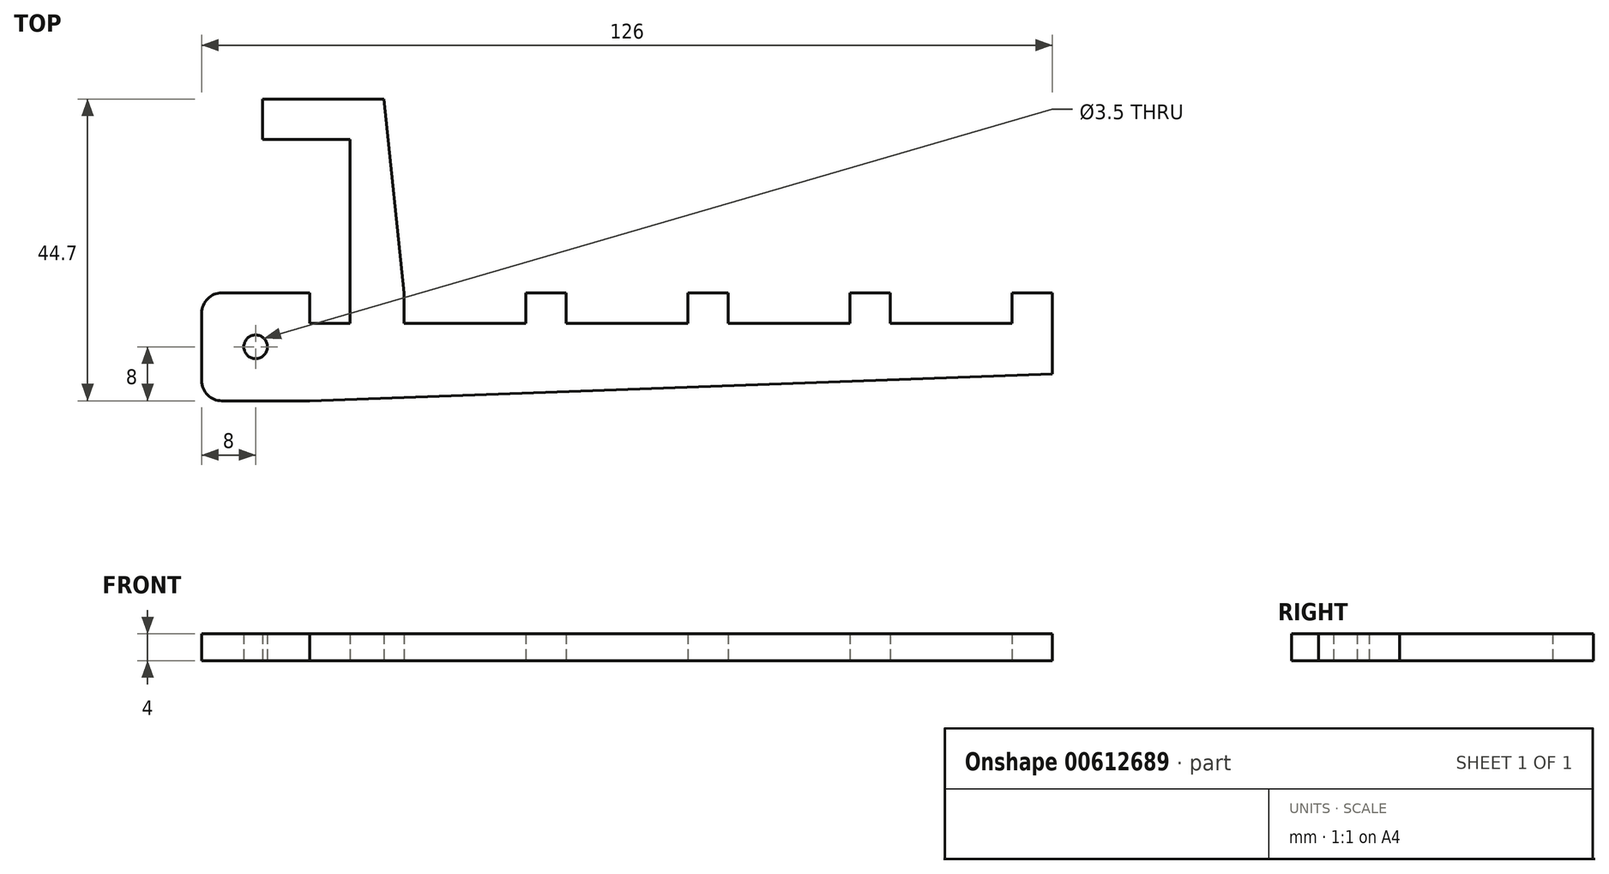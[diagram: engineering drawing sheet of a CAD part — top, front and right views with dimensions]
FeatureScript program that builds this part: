
annotation { "Feature Type Name" : "Feature", "Feature Type Description" : "" }
export const myFeature = defineFeature(function(context is Context, id is Id, definition is map)
    precondition{}
    {
        {
            var Q0;
            Q0=qCreatedBy(makeId("Top.planeOp"),FACE);
            var sketch = newSketch(context, id + "F0", { "sketchPlane" : qUnion([Q0])});
            skLineSegment(sketch, "E0", {"start": v(-36, 22.35) * mm, "end": v(-54, 22.35) * mm});
            skLineSegment(sketch, "E1", {"start": v(-41, 16.35) * mm, "end": v(-54, 16.35) * mm});
            skLineSegment(sketch, "E2", {"start": v(39, -6.35) * mm, "end": v(33, -6.35) * mm});
            skLineSegment(sketch, "E3", {"start": v(63, -6.35) * mm, "end": v(57, -6.35) * mm});
            skLineSegment(sketch, "E4", {"start": v(15, -6.35) * mm, "end": v(9, -6.35) * mm});
            skLineSegment(sketch, "E5", {"start": v(-9, -6.35) * mm, "end": v(-15, -6.35) * mm});
            skLineSegment(sketch, "E6", {"start": v(-47, -6.35) * mm, "end": v(-60, -6.35) * mm});
            skLineSegment(sketch, "E7", {"start": v(63, -6.35) * mm, "end": v(63, -18.35) * mm});
            skLineSegment(sketch, "E8", {"start": v(-41, 16.35) * mm, "end": v(-41, -10.85) * mm});
            skLineSegment(sketch, "E9", {"start": v(-54, 22.35) * mm, "end": v(-54, 16.35) * mm});
            skLineSegment(sketch, "E10", {"start": v(-36, 22.35) * mm, "end": v(-33, -6.35) * mm});
            skLineSegment(sketch, "E11", {"start": v(33, -10.85) * mm, "end": v(15, -10.85) * mm});
            skLineSegment(sketch, "E12", {"start": v(57, -10.85) * mm, "end": v(39, -10.85) * mm});
            skLineSegment(sketch, "E13", {"start": v(9, -10.85) * mm, "end": v(-9, -10.85) * mm});
            skLineSegment(sketch, "E14", {"start": v(-15, -10.85) * mm, "end": v(-33, -10.85) * mm});
            skLineSegment(sketch, "E15", {"start": v(-41, -10.85) * mm, "end": v(-47, -10.85) * mm});
            skLineSegment(sketch, "E16", {"start": v(-47, -6.35) * mm, "end": v(-47, -10.85) * mm});
            skLineSegment(sketch, "E17", {"start": v(-33, -6.35) * mm, "end": v(-33, -10.85) * mm});
            skLineSegment(sketch, "E18", {"start": v(57, -6.35) * mm, "end": v(57, -10.85) * mm});
            skLineSegment(sketch, "E19", {"start": v(39, -6.35) * mm, "end": v(39, -10.85) * mm});
            skLineSegment(sketch, "E20", {"start": v(-15, -6.35) * mm, "end": v(-15, -10.85) * mm});
            skLineSegment(sketch, "E21", {"start": v(-9, -6.35) * mm, "end": v(-9, -10.85) * mm});
            skLineSegment(sketch, "E22", {"start": v(33, -6.35) * mm, "end": v(33, -10.85) * mm});
            skLineSegment(sketch, "E23", {"start": v(15, -6.35) * mm, "end": v(15, -10.85) * mm});
            skLineSegment(sketch, "E24", {"start": v(9, -6.35) * mm, "end": v(9, -10.85) * mm});
            skLineSegment(sketch, "E25", {"start": v(-63, -9.35) * mm, "end": v(-63, -19.35) * mm});
            skLineSegment(sketch, "E26", {"start": v(-47, -22.35) * mm, "end": v(-60, -22.35) * mm});
            skArc(sketch, "E27", {"start": v(-60, -6.35) * mm, "mid": v(-62.12, -7.23) * mm, "end": v(-63, -9.35) * mm});
            skArc(sketch, "E28", {"start": v(-63, -19.35) * mm, "mid": v(-62.12, -21.47) * mm, "end": v(-60, -22.35) * mm});
            skLineSegment(sketch, "E29", {"start": v(-47, -22.35) * mm, "end": v(63, -18.35) * mm});
            skCircle(sketch, "E30", {"center": v(-55, -14.35) * mm, "radius": 1.75 * mm});
            skSolve(sketch);
        }
        {
            var Q0;
            Q0=makeQuery(id+"F0.imprint","IMPRINT",FACE,{"disambiguationData":[TD([[makeQuery(id+"F0.imprint","IMPRINT",EDGE,{"derivedFrom":sQuery(id+"F0.wireOp",EDGE,"E0")}),1.0]])]});
            extrude(context, id + "F1", {"entities" : qUnion([Q0]), "depth" : 4 * mm, "offsetDistance" : 25 * mm});
        }
    });
